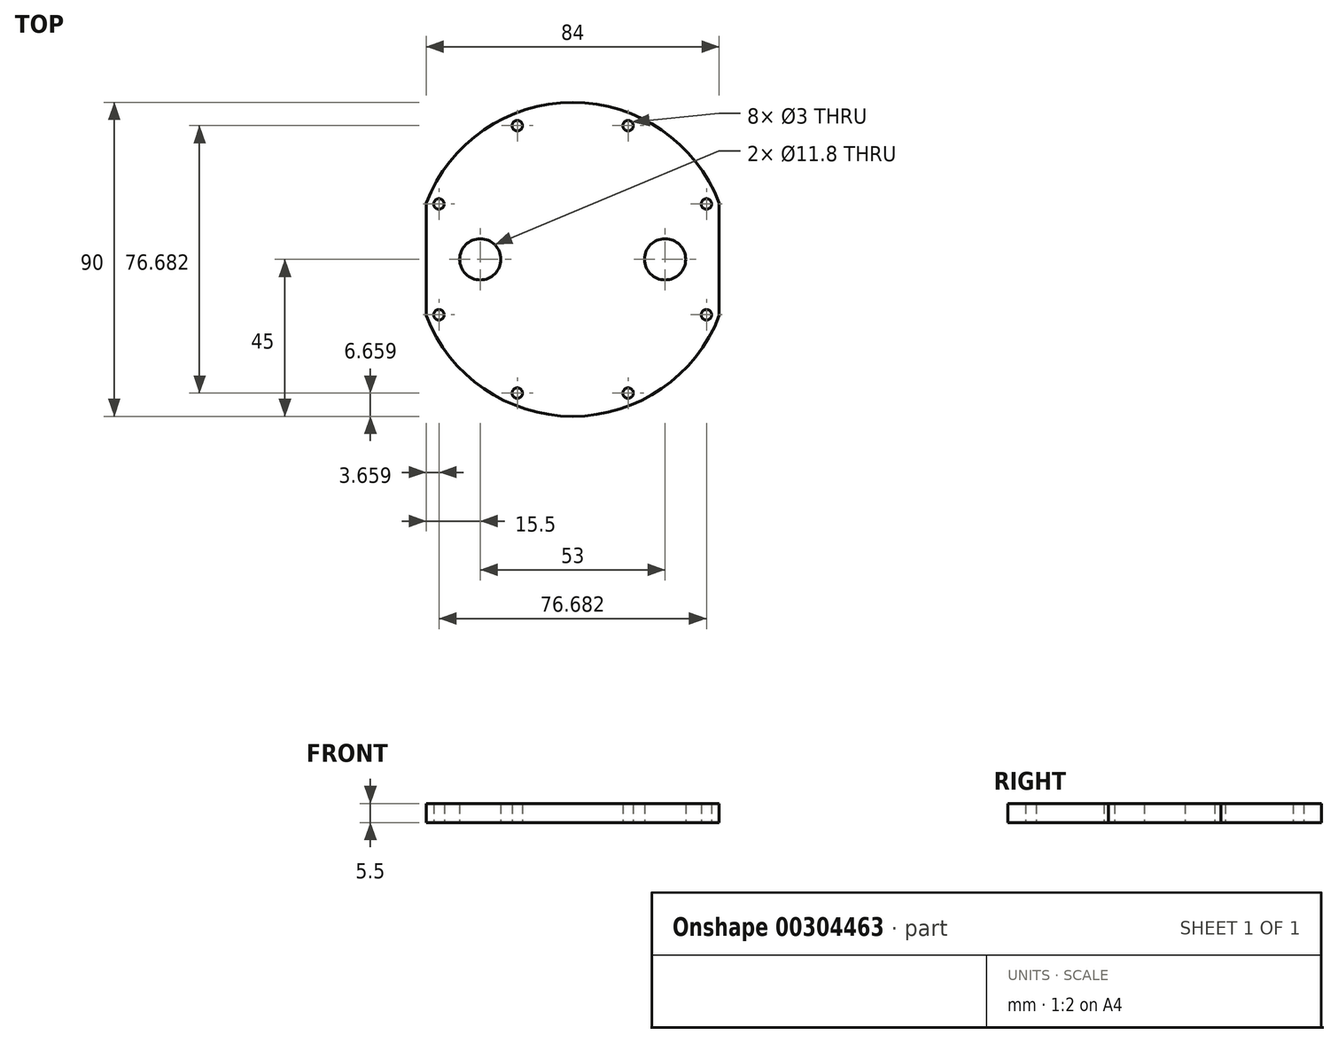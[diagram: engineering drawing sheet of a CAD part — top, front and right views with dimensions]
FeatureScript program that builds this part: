
annotation { "Feature Type Name" : "Feature", "Feature Type Description" : "" }
export const myFeature = defineFeature(function(context is Context, id is Id, definition is map)
    precondition{}
    {
        {
            var Q0;
            Q0=qCreatedBy(makeId("Top.planeOp"),FACE);
            var sketch = newSketch(context, id + "F0", { "sketchPlane" : qUnion([Q0])});
            skCircle(sketch, "E0", {"center": v(0, 0) * mm, "radius": 41.5 * mm, "construction": true});
            skLineSegment(sketch, "E1", {"start": v(-70.37, 0) * mm, "end": v(66.46, 0) * mm, "construction": true});
            skLineSegment(sketch, "E2", {"start": v(0, 0) * mm, "end": v(-65.17, 27) * mm, "construction": true});
            skCircle(sketch, "E3", {"center": v(-38.34, 15.88) * mm, "radius": 1.5 * mm});
            skCircle(sketch, "E4.1.0", {"center": v(-38.34, -15.88) * mm, "radius": 1.5 * mm});
            skCircle(sketch, "E4.2.0", {"center": v(-15.88, -38.34) * mm, "radius": 1.5 * mm});
            skCircle(sketch, "E4.3.0", {"center": v(15.88, -38.34) * mm, "radius": 1.5 * mm});
            skCircle(sketch, "E4.4.0", {"center": v(38.34, -15.88) * mm, "radius": 1.5 * mm});
            skCircle(sketch, "E4.5.0", {"center": v(38.34, 15.88) * mm, "radius": 1.5 * mm});
            skCircle(sketch, "E4.6.0", {"center": v(15.88, 38.34) * mm, "radius": 1.5 * mm});
            skCircle(sketch, "E4.7.0", {"center": v(-15.88, 38.34) * mm, "radius": 1.5 * mm});
            skCircle(sketch, "E5", {"center": v(-26.5, 0) * mm, "radius": 5.9 * mm});
            skCircle(sketch, "E6", {"center": v(26.5, 0) * mm, "radius": 5.9 * mm});
            skCircle(sketch, "E7", {"center": v(-26.5, 0) * mm, "radius": 6.8 * mm, "construction": true});
            skCircle(sketch, "E8", {"center": v(26.5, 0) * mm, "radius": 6.8 * mm, "construction": true});
            skCircle(sketch, "E9", {"center": v(0, 0) * mm, "radius": 57.5 * mm, "construction": true});
            skArc(sketch, "E10", {"start": v(42, -16.16) * mm, "mid": v(0, -45) * mm, "end": v(-42, -16.16) * mm});
            skLineSegment(sketch, "E11", {"start": v(42, 16.16) * mm, "end": v(42, -16.16) * mm});
            skLineSegment(sketch, "E12", {"start": v(-42, 16.16) * mm, "end": v(-42, -16.16) * mm});
            skPoint(sketch, "E13", {"position": v(-42, 0) * mm});
            skPoint(sketch, "E14", {"position": v(42, 0) * mm});
            skLineSegment(sketch, "E15", {"start": v(0, 0) * mm, "end": v(0, 69.32) * mm, "construction": true});
            skArc(sketch, "E16", {"start": v(-42, 16.16) * mm, "mid": v(0, 45) * mm, "end": v(42, 16.16) * mm});
            skSolve(sketch);
        }
        {
            var Q0;
            Q0 = qSketchRegion(id + "F0", true);
            extrude(context, id + "F1", {"entities" : qUnion([Q0]), "depth" : 5.5 * mm, "offsetDistance" : 25 * mm});
        }
    });
